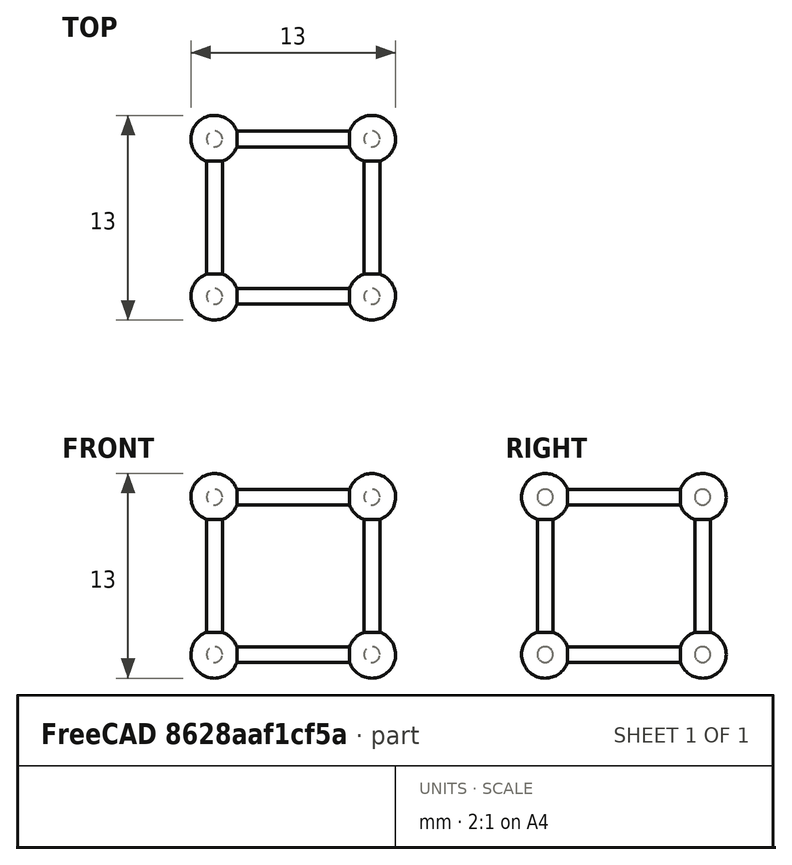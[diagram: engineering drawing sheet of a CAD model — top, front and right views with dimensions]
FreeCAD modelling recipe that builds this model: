
FCSTD DOCUMENT  (FreeCAD 0.21R33771 (Git))
Label: test
License: All rights reserved
LicenseURL: http://en.wikipedia.org/wiki/All_rights_reserved
objects: Part::Cylinder×12, Part::Sphere×8, Part::MultiFuse×1
note: 21 computed .brp shape members not serialized (recipe doc carries the construction recipe); baked Part::Feature solids carry a one-line shape summary decoded from their .brp

FEATURE [Part::Sphere] Sphere
  Angle1 = -90
  Angle2 = 90
  Angle3 = 360
  AttacherType = Attacher::AttachEngine3D
  Radius = 1.5
FEATURE [Part::Sphere] Sphere001
  Angle1 = -90
  Angle2 = 90
  Angle3 = 360
  AttacherType = Attacher::AttachEngine3D
  Placement = pos=(0,10,0) rot=(0,0,1;0rad)
  Radius = 1.5
FEATURE [Part::Sphere] Sphere002
  Angle1 = -90
  Angle2 = 90
  Angle3 = 360
  AttacherType = Attacher::AttachEngine3D
  Placement = pos=(10,10,0) rot=(0,0,1;0rad)
  Radius = 1.5
FEATURE [Part::Sphere] Sphere003
  Angle1 = -90
  Angle2 = 90
  Angle3 = 360
  AttacherType = Attacher::AttachEngine3D
  Placement = pos=(10,0,0) rot=(0,0,1;0rad)
  Radius = 1.5
FEATURE [Part::Sphere] Sphere004
  Angle1 = -90
  Angle2 = 90
  Angle3 = 360
  AttacherType = Attacher::AttachEngine3D
  Placement = pos=(0,0,10) rot=(0,0,1;0rad)
  Radius = 1.5
FEATURE [Part::Sphere] Sphere005
  Angle1 = -90
  Angle2 = 90
  Angle3 = 360
  AttacherType = Attacher::AttachEngine3D
  Placement = pos=(0,10,10) rot=(0,0,1;0rad)
  Radius = 1.5
FEATURE [Part::Sphere] Sphere006
  Angle1 = -90
  Angle2 = 90
  Angle3 = 360
  AttacherType = Attacher::AttachEngine3D
  Placement = pos=(10,10,10) rot=(0,0,1;0rad)
  Radius = 1.5
FEATURE [Part::Sphere] Sphere007
  Angle1 = -90
  Angle2 = 90
  Angle3 = 360
  AttacherType = Attacher::AttachEngine3D
  Placement = pos=(10,0,10) rot=(0,0,1;0rad)
  Radius = 1.5
FEATURE [Part::Cylinder] Cylinder
  Angle = 360
  AttacherType = Attacher::AttachEngine3D
  FirstAngle = 0
  Height = 10
  Placement = pos=(0,0,0) rot=(-10,0,0;1.5708rad)
  Radius = 0.5
  SecondAngle = 0
FEATURE [Part::Cylinder] Cylinder001
  Angle = 360
  AttacherType = Attacher::AttachEngine3D
  FirstAngle = 0
  Height = 10
  Placement = pos=(0,0,10) rot=(-10,0,0;1.5708rad)
  Radius = 0.5
  SecondAngle = 0
FEATURE [Part::Cylinder] Cylinder002
  Angle = 360
  AttacherType = Attacher::AttachEngine3D
  FirstAngle = 0
  Height = 10
  Radius = 0.5
  SecondAngle = 0
FEATURE [Part::Cylinder] Cylinder003
  Angle = 360
  AttacherType = Attacher::AttachEngine3D
  FirstAngle = 0
  Height = 10
  Placement = pos=(0,10,0) rot=(0,10,0;1.5708rad)
  Radius = 0.5
  SecondAngle = 0
FEATURE [Part::Cylinder] Cylinder004
  Angle = 360
  AttacherType = Attacher::AttachEngine3D
  FirstAngle = 0
  Height = 10
  Placement = pos=(0,10,10) rot=(0,10,0;1.5708rad)
  Radius = 0.5
  SecondAngle = 0
FEATURE [Part::Cylinder] Cylinder005
  Angle = 360
  AttacherType = Attacher::AttachEngine3D
  FirstAngle = 0
  Height = 10
  Placement = pos=(0,10,0) rot=(0,0,1;0rad)
  Radius = 0.5
  SecondAngle = 0
FEATURE [Part::Cylinder] Cylinder006
  Angle = 360
  AttacherType = Attacher::AttachEngine3D
  FirstAngle = 0
  Height = 10
  Placement = pos=(10,10,0) rot=(10,0,0;1.5708rad)
  Radius = 0.5
  SecondAngle = 0
FEATURE [Part::Cylinder] Cylinder007
  Angle = 360
  AttacherType = Attacher::AttachEngine3D
  FirstAngle = 0
  Height = 10
  Placement = pos=(10,10,10) rot=(10,0,0;1.5708rad)
  Radius = 0.5
  SecondAngle = 0
FEATURE [Part::Cylinder] Cylinder008
  Angle = 360
  AttacherType = Attacher::AttachEngine3D
  FirstAngle = 0
  Height = 10
  Placement = pos=(10,10,0) rot=(0,0,1;0rad)
  Radius = 0.5
  SecondAngle = 0
FEATURE [Part::Cylinder] Cylinder009
  Angle = 360
  AttacherType = Attacher::AttachEngine3D
  FirstAngle = 0
  Height = 10
  Placement = pos=(10,0,0) rot=(0,-10,0;1.5708rad)
  Radius = 0.5
  SecondAngle = 0
FEATURE [Part::Cylinder] Cylinder010
  Angle = 360
  AttacherType = Attacher::AttachEngine3D
  FirstAngle = 0
  Height = 10
  Placement = pos=(10,0,10) rot=(0,-10,0;1.5708rad)
  Radius = 0.5
  SecondAngle = 0
FEATURE [Part::Cylinder] Cylinder011
  Angle = 360
  AttacherType = Attacher::AttachEngine3D
  FirstAngle = 0
  Height = 10
  Placement = pos=(10,0,0) rot=(0,0,1;0rad)
  Radius = 0.5
  SecondAngle = 0
FEATURE [Part::MultiFuse] Fusion
  Shapes = -> [Sphere,Sphere001,Sphere002,Sphere003,Sphere004,Sphere005,Sphere006,Sphere007,Cylinder,Cylinder001,Cylinder002,Cylinder003,Cylinder004,Cylinder005,Cylinder006,Cylinder007,Cylinder008,Cylinder009,Cylinder010,Cylinder011]
